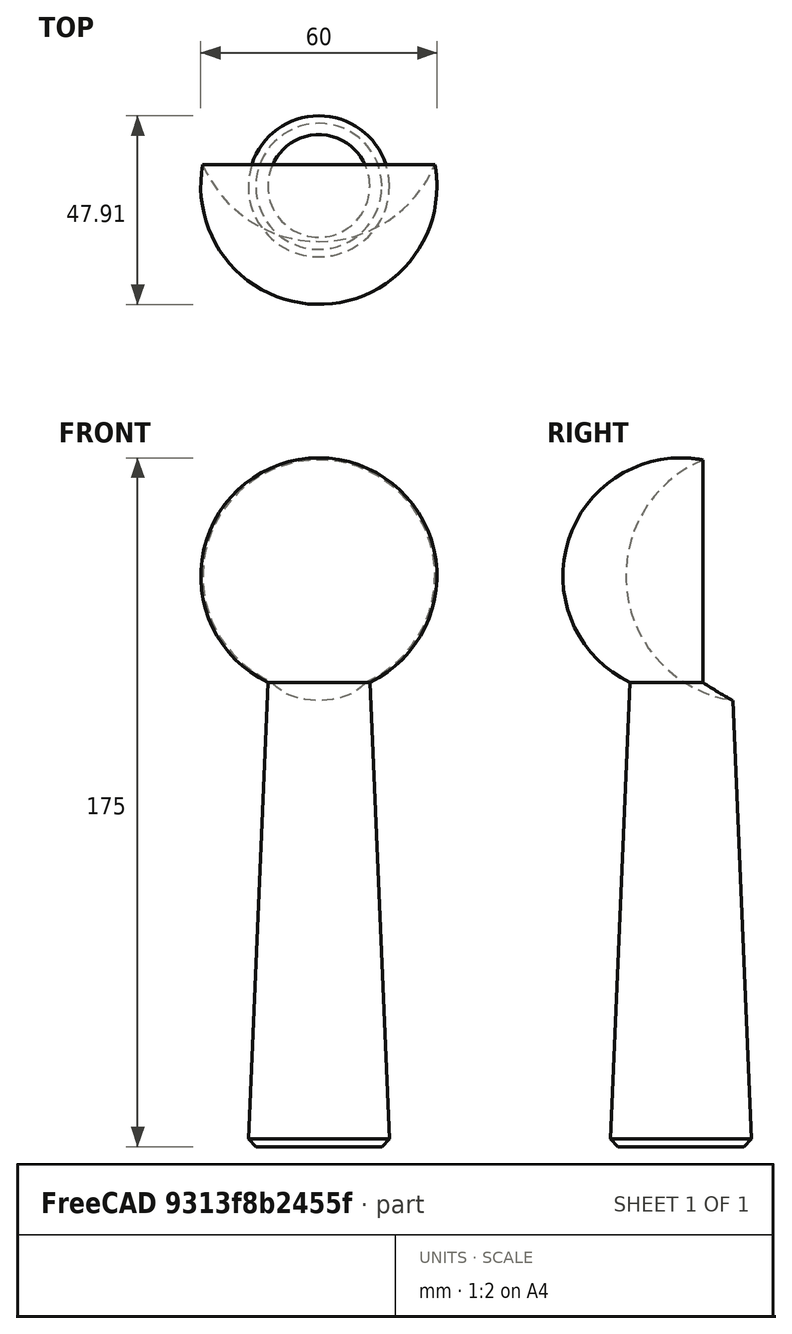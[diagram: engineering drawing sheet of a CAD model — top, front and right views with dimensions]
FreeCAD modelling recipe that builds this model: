
FCSTD DOCUMENT  (FreeCAD 0.19R)
Label: Scoop
License: All rights reserved
LicenseURL: http://en.wikipedia.org/wiki/All_rights_reserved
objects: Part::Sphere×2, PartDesign::Body×1, Part::Cone×1, Part::MultiFuse×1, Part::Cut×1, Part::Chamfer×1, Mesh::Feature×1
note: 7 computed .brp shape members not serialized (recipe doc carries the construction recipe); baked Part::Feature solids carry a one-line shape summary decoded from their .brp

FEATURE [PartDesign::Body] Body
  Origin = -> Origin
FEATURE [Part::Cone] Cone
  Angle = 360
  AttacherType = Attacher::AttachEngine3D
  Height = 140
  Radius1 = 18
  Radius2 = 12
FEATURE [Part::Sphere] Sphere
  Angle1 = -90
  Angle2 = 90
  Angle3 = 360
  AttacherType = Attacher::AttachEngine3D
  Placement = pos=(0,0,145) rot=(0,0,1;0rad)
  Radius = 30
FEATURE [Part::Sphere] Sphere001
  Angle1 = -90
  Angle2 = 90
  Angle3 = 360
  AttacherType = Attacher::AttachEngine3D
  Placement = pos=(0,18,145) rot=(0,0,1;0rad)
  Radius = 32
FEATURE [Part::MultiFuse] Fusion
  Shapes = -> [Cone,Sphere]
FEATURE [Part::Cut] Cut
  Base = -> Fusion
  Tool = -> Sphere001
FEATURE [Part::Chamfer] Chamfer
  Base = -> Cut
  Edges = 1 edges r=2: [Edge2]
FEATURE [Mesh::Feature] Mesh  label="Chamfer (Meshed)"
